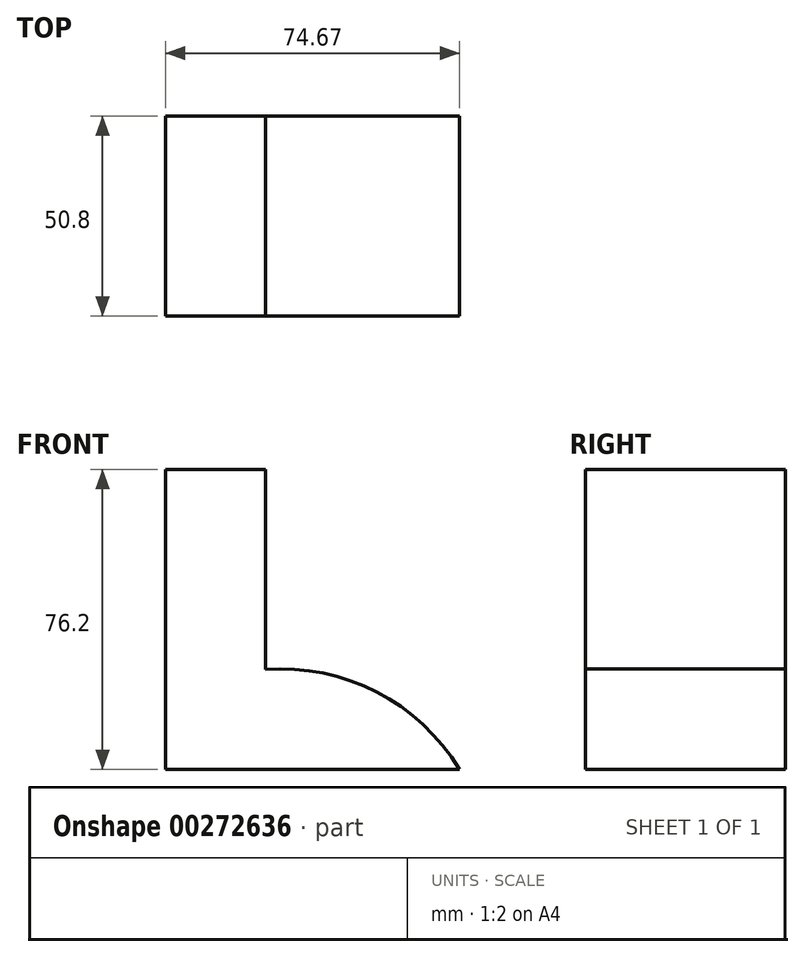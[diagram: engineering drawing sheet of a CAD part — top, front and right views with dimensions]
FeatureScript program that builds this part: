
annotation { "Feature Type Name" : "Feature", "Feature Type Description" : "" }
export const myFeature = defineFeature(function(context is Context, id is Id, definition is map)
    precondition{}
    {
        {
            var Q0;
            Q0=qCreatedBy(makeId("Front.planeOp"),FACE);
            var sketch = newSketch(context, id + "F0", { "sketchPlane" : qUnion([Q0])});
            skLineSegment(sketch, "E0", {"start": v(-41.63, 35.53) * mm, "end": v(-41.63, -40.67) * mm});
            skLineSegment(sketch, "E1", {"start": v(-41.63, -40.67) * mm, "end": v(34.57, -40.67) * mm});
            skLineSegment(sketch, "E2", {"start": v(-41.63, 35.53) * mm, "end": v(-16.23, 35.53) * mm});
            skLineSegment(sketch, "E3", {"start": v(-16.23, 35.53) * mm, "end": v(-16.23, -15.27) * mm});
            skArc(sketch, "E4", {"start": v(33.04, -40.67) * mm, "mid": v(12, -21) * mm, "end": v(-16.23, -15.27) * mm});
            skSolve(sketch);
        }
        {
            var Q0;
            Q0 = qSketchRegion(id + "F0", true);
            extrude(context, id + "F1", {"entities" : qUnion([Q0]), "depth" : 50.8 * mm});
        }
    });
